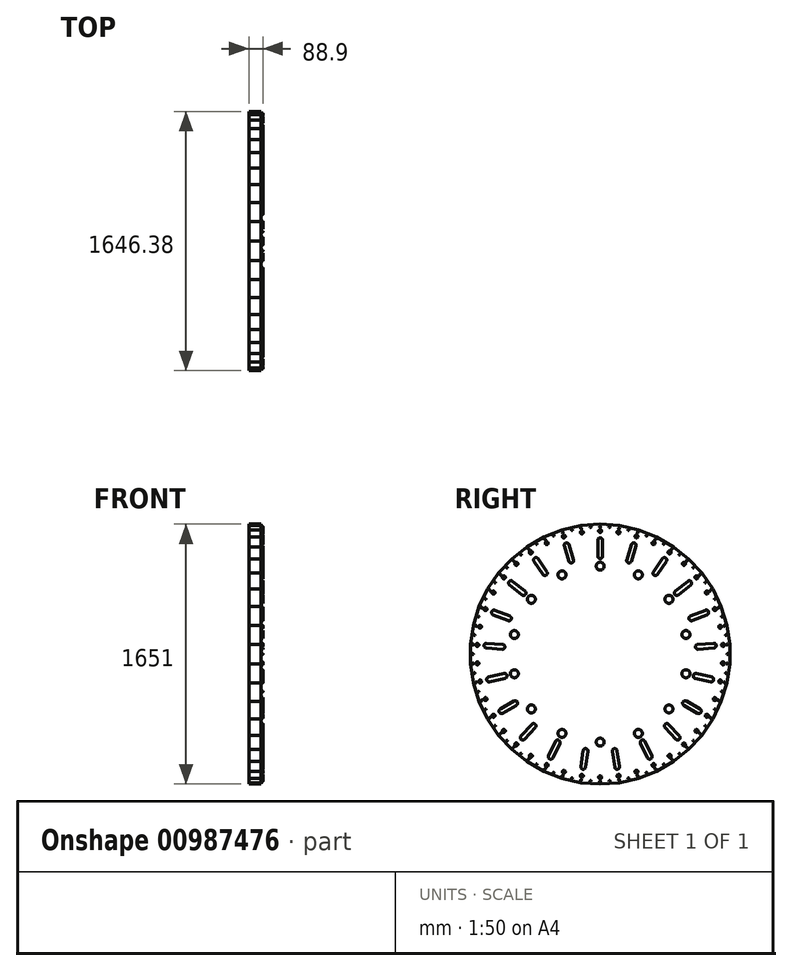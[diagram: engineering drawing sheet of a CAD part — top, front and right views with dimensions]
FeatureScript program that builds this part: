
annotation { "Feature Type Name" : "Feature", "Feature Type Description" : "" }
export const myFeature = defineFeature(function(context is Context, id is Id, definition is map)
    precondition{}
    {
        {
            var Q0;
            Q0=qCreatedBy(makeId("Right.planeOp"),FACE);
            var sketch = newSketch(context, id + "F0", { "sketchPlane" : qUnion([Q0])});
            skCircle(sketch, "E0.cCircle", {"center": v(0, 0) * mm, "radius": 825.5 * mm, "construction": true});
            skLineSegment(sketch, "E0.0", {"start": v(714.9, 412.75) * mm, "end": v(768.44, 301.59) * mm});
            skLineSegment(sketch, "E0.1", {"start": v(768.44, 301.59) * mm, "end": v(804.8, 183.7) * mm});
            skLineSegment(sketch, "E0.2", {"start": v(804.8, 183.7) * mm, "end": v(823.2, 61.69) * mm});
            skLineSegment(sketch, "E0.3", {"start": v(823.2, 61.69) * mm, "end": v(823.2, -61.69) * mm});
            skLineSegment(sketch, "E0.4", {"start": v(823.2, -61.69) * mm, "end": v(804.8, -183.7) * mm});
            skLineSegment(sketch, "E0.5", {"start": v(804.8, -183.7) * mm, "end": v(768.44, -301.59) * mm});
            skLineSegment(sketch, "E0.6", {"start": v(768.44, -301.59) * mm, "end": v(714.9, -412.75) * mm});
            skLineSegment(sketch, "E0.7", {"start": v(714.9, -412.75) * mm, "end": v(645.4, -514.7) * mm});
            skLineSegment(sketch, "E0.8", {"start": v(645.4, -514.7) * mm, "end": v(561.48, -605.13) * mm});
            skLineSegment(sketch, "E0.9", {"start": v(561.48, -605.13) * mm, "end": v(465.02, -682.06) * mm});
            skLineSegment(sketch, "E0.10", {"start": v(465.02, -682.06) * mm, "end": v(358.17, -743.75) * mm});
            skLineSegment(sketch, "E0.11", {"start": v(358.17, -743.75) * mm, "end": v(243.32, -788.83) * mm});
            skLineSegment(sketch, "E0.12", {"start": v(243.32, -788.83) * mm, "end": v(123.03, -816.28) * mm});
            skLineSegment(sketch, "E0.13", {"start": v(123.03, -816.28) * mm, "end": v(0, -825.5) * mm});
            skLineSegment(sketch, "E0.14", {"start": v(0, -825.5) * mm, "end": v(-123.03, -816.28) * mm});
            skLineSegment(sketch, "E0.15", {"start": v(-123.03, -816.28) * mm, "end": v(-243.32, -788.83) * mm});
            skLineSegment(sketch, "E0.16", {"start": v(-243.32, -788.83) * mm, "end": v(-358.17, -743.75) * mm});
            skLineSegment(sketch, "E0.17", {"start": v(-358.17, -743.75) * mm, "end": v(-465.02, -682.06) * mm});
            skLineSegment(sketch, "E0.18", {"start": v(-465.02, -682.06) * mm, "end": v(-561.48, -605.13) * mm});
            skLineSegment(sketch, "E0.19", {"start": v(-561.48, -605.13) * mm, "end": v(-645.4, -514.7) * mm});
            skLineSegment(sketch, "E0.20", {"start": v(-645.4, -514.7) * mm, "end": v(-714.9, -412.75) * mm});
            skLineSegment(sketch, "E0.21", {"start": v(-714.9, -412.75) * mm, "end": v(-768.44, -301.59) * mm});
            skLineSegment(sketch, "E0.22", {"start": v(-768.44, -301.59) * mm, "end": v(-804.8, -183.7) * mm});
            skLineSegment(sketch, "E0.23", {"start": v(-804.8, -183.7) * mm, "end": v(-823.2, -61.69) * mm});
            skLineSegment(sketch, "E0.24", {"start": v(-823.2, -61.69) * mm, "end": v(-823.2, 61.69) * mm});
            skLineSegment(sketch, "E0.25", {"start": v(-823.2, 61.69) * mm, "end": v(-804.8, 183.7) * mm});
            skLineSegment(sketch, "E0.26", {"start": v(-804.8, 183.7) * mm, "end": v(-768.44, 301.59) * mm});
            skLineSegment(sketch, "E0.27", {"start": v(-768.44, 301.59) * mm, "end": v(-714.9, 412.75) * mm});
            skLineSegment(sketch, "E0.28", {"start": v(-714.9, 412.75) * mm, "end": v(-645.4, 514.7) * mm});
            skLineSegment(sketch, "E0.29", {"start": v(-645.4, 514.7) * mm, "end": v(-561.48, 605.13) * mm});
            skLineSegment(sketch, "E0.30", {"start": v(-561.48, 605.13) * mm, "end": v(-465.02, 682.06) * mm});
            skLineSegment(sketch, "E0.31", {"start": v(-465.02, 682.06) * mm, "end": v(-358.17, 743.75) * mm});
            skLineSegment(sketch, "E0.32", {"start": v(-358.17, 743.75) * mm, "end": v(-243.32, 788.83) * mm});
            skLineSegment(sketch, "E0.33", {"start": v(-243.32, 788.83) * mm, "end": v(-123.03, 816.28) * mm});
            skLineSegment(sketch, "E0.34", {"start": v(-123.03, 816.28) * mm, "end": v(0, 825.5) * mm});
            skLineSegment(sketch, "E0.35", {"start": v(0, 825.5) * mm, "end": v(123.03, 816.28) * mm});
            skLineSegment(sketch, "E0.36", {"start": v(123.03, 816.28) * mm, "end": v(243.32, 788.83) * mm});
            skLineSegment(sketch, "E0.37", {"start": v(243.32, 788.83) * mm, "end": v(358.17, 743.75) * mm});
            skLineSegment(sketch, "E0.38", {"start": v(358.17, 743.75) * mm, "end": v(465.02, 682.06) * mm});
            skLineSegment(sketch, "E0.39", {"start": v(465.02, 682.06) * mm, "end": v(561.48, 605.13) * mm});
            skLineSegment(sketch, "E0.40", {"start": v(561.48, 605.13) * mm, "end": v(645.4, 514.7) * mm});
            skLineSegment(sketch, "E0.41", {"start": v(645.4, 514.7) * mm, "end": v(714.9, 412.75) * mm});
            skCircle(sketch, "E1", {"center": v(2658.03, 0) * mm, "radius": 825.5 * mm});
            skLineSegment(sketch, "E2", {"start": v(0, 825.5) * mm, "end": v(0, 0) * mm, "construction": true});
            skSolve(sketch);
        }
        {
            var Q0;
            Q0=makeQuery(id+"F0.imprint","IMPRINT",FACE,{"disambiguationData":[TD([[makeQuery(id+"F0.imprint","IMPRINT",EDGE,{"derivedFrom":sQuery(id+"F0.wireOp",EDGE,"E0.0")}),-1.0]])]});
            extrude(context, id + "F1", {"entities" : qUnion([Q0]), "depth" : 76.2 * mm, "offsetDistance" : 25.4 * mm});
        }
        {
            var Q0;
            Q0=makeQuery(id+"F1.opExtrude","CAP_FACE",FACE,{"disambiguationData":[OSD([sQuery(id+"F0.wireOp",EDGE,"E0.0"),sQuery(id+"F0.wireOp",EDGE,"E0.1"),sQuery(id+"F0.wireOp",EDGE,"E0.2"),sQuery(id+"F0.wireOp",EDGE,"E0.3"),sQuery(id+"F0.wireOp",EDGE,"E0.4"),sQuery(id+"F0.wireOp",EDGE,"E0.5"),sQuery(id+"F0.wireOp",EDGE,"E0.6"),sQuery(id+"F0.wireOp",EDGE,"E0.7"),sQuery(id+"F0.wireOp",EDGE,"E0.8"),sQuery(id+"F0.wireOp",EDGE,"E0.9"),sQuery(id+"F0.wireOp",EDGE,"E0.10"),sQuery(id+"F0.wireOp",EDGE,"E0.11"),sQuery(id+"F0.wireOp",EDGE,"E0.12"),sQuery(id+"F0.wireOp",EDGE,"E0.13"),sQuery(id+"F0.wireOp",EDGE,"E0.14"),sQuery(id+"F0.wireOp",EDGE,"E0.15"),sQuery(id+"F0.wireOp",EDGE,"E0.16"),sQuery(id+"F0.wireOp",EDGE,"E0.17"),sQuery(id+"F0.wireOp",EDGE,"E0.18"),sQuery(id+"F0.wireOp",EDGE,"E0.19"),sQuery(id+"F0.wireOp",EDGE,"E0.20"),sQuery(id+"F0.wireOp",EDGE,"E0.21"),sQuery(id+"F0.wireOp",EDGE,"E0.22"),sQuery(id+"F0.wireOp",EDGE,"E0.23"),sQuery(id+"F0.wireOp",EDGE,"E0.24"),sQuery(id+"F0.wireOp",EDGE,"E0.25"),sQuery(id+"F0.wireOp",EDGE,"E0.26"),sQuery(id+"F0.wireOp",EDGE,"E0.27"),sQuery(id+"F0.wireOp",EDGE,"E0.28"),sQuery(id+"F0.wireOp",EDGE,"E0.29"),sQuery(id+"F0.wireOp",EDGE,"E0.30"),sQuery(id+"F0.wireOp",EDGE,"E0.31"),sQuery(id+"F0.wireOp",EDGE,"E0.32"),sQuery(id+"F0.wireOp",EDGE,"E0.33"),sQuery(id+"F0.wireOp",EDGE,"E0.34"),sQuery(id+"F0.wireOp",EDGE,"E0.35"),sQuery(id+"F0.wireOp",EDGE,"E0.36"),sQuery(id+"F0.wireOp",EDGE,"E0.37"),sQuery(id+"F0.wireOp",EDGE,"E0.38"),sQuery(id+"F0.wireOp",EDGE,"E0.39"),sQuery(id+"F0.wireOp",EDGE,"E0.40"),sQuery(id+"F0.wireOp",EDGE,"E0.41")])],"isStart":false});
            var sketch = newSketch(context, id + "F2", { "sketchPlane" : qUnion([Q0])});
            skLineSegment(sketch, "E3", {"start": v(0, 622.3) * mm, "end": v(0, 723.9) * mm, "construction": true});
            skLineSegment(sketch, "E4", {"start": v(0, 0) * mm, "end": v(0, 622.3) * mm, "construction": true});
            skLineSegment(sketch, "E5", {"start": v(15.24, 723.9) * mm, "end": v(15.24, 622.3) * mm});
            skArc(sketch, "E6", {"start": v(-15.24, 723.9) * mm, "mid": v(0, 708.66) * mm, "end": v(15.24, 723.9) * mm, "construction": true});
            skArc(sketch, "E7", {"start": v(15.24, 723.9) * mm, "mid": v(10.78, 734.68) * mm, "end": v(0, 739.14) * mm});
            skArc(sketch, "E8", {"start": v(15.23, 622.91) * mm, "mid": v(-0.3, 637.54) * mm, "end": v(-15.24, 622.3) * mm, "construction": true});
            skArc(sketch, "E9", {"start": v(-15.24, 622.3) * mm, "mid": v(0.3, 607.06) * mm, "end": v(15.23, 622.91) * mm});
            skLineSegment(sketch, "E10.MirrorCS", {"start": v(-15.24, 723.9) * mm, "end": v(-15.24, 622.3) * mm});
            skLineSegment(sketch, "E11.1.0", {"start": v(198.81, 696.23) * mm, "end": v(168.86, 599.15) * mm});
            skArc(sketch, "E11.1.1", {"start": v(227.94, 687.25) * mm, "mid": v(217.87, 706.3) * mm, "end": v(198.81, 696.23) * mm});
            skLineSegment(sketch, "E11.1.2", {"start": v(227.94, 687.25) * mm, "end": v(197.99, 590.16) * mm});
            skArc(sketch, "E11.1.3", {"start": v(168.86, 599.15) * mm, "mid": v(179.23, 580) * mm, "end": v(198.16, 590.75) * mm});
            skLineSegment(sketch, "E11.2.0", {"start": v(395.2, 606.7) * mm, "end": v(337.96, 522.75) * mm});
            skArc(sketch, "E11.2.1", {"start": v(420.38, 589.53) * mm, "mid": v(416.37, 610.7) * mm, "end": v(395.2, 606.7) * mm});
            skLineSegment(sketch, "E11.2.2", {"start": v(420.38, 589.53) * mm, "end": v(363.15, 505.58) * mm});
            skArc(sketch, "E11.2.3", {"start": v(337.96, 522.75) * mm, "mid": v(342.22, 501.4) * mm, "end": v(363.48, 506.1) * mm});
            skLineSegment(sketch, "E11.3.0", {"start": v(556.47, 463.26) * mm, "end": v(477.03, 399.91) * mm});
            skArc(sketch, "E11.3.1", {"start": v(575.47, 439.43) * mm, "mid": v(577.88, 460.85) * mm, "end": v(556.47, 463.26) * mm});
            skLineSegment(sketch, "E11.3.2", {"start": v(575.47, 439.43) * mm, "end": v(496.04, 376.08) * mm});
            skArc(sketch, "E11.3.3", {"start": v(477.03, 399.91) * mm, "mid": v(474.81, 378.26) * mm, "end": v(496.5, 376.47) * mm});
            skLineSegment(sketch, "E11.4.0", {"start": v(668.3, 278.66) * mm, "end": v(573.71, 241.54) * mm});
            skArc(sketch, "E11.4.1", {"start": v(679.43, 250.28) * mm, "mid": v(688.05, 270.04) * mm, "end": v(668.3, 278.66) * mm});
            skLineSegment(sketch, "E11.4.2", {"start": v(679.43, 250.28) * mm, "end": v(584.85, 213.17) * mm});
            skArc(sketch, "E11.4.3", {"start": v(573.71, 241.54) * mm, "mid": v(565.21, 221.5) * mm, "end": v(585.42, 213.4) * mm});
            skLineSegment(sketch, "E11.5.0", {"start": v(720.74, 69.3) * mm, "end": v(619.42, 61.7) * mm});
            skArc(sketch, "E11.5.1", {"start": v(723.01, 38.9) * mm, "mid": v(737.07, 55.24) * mm, "end": v(720.74, 69.3) * mm});
            skLineSegment(sketch, "E11.5.2", {"start": v(723.01, 38.9) * mm, "end": v(621.7, 31.3) * mm});
            skArc(sketch, "E11.5.3", {"start": v(619.42, 61.7) * mm, "mid": v(605.39, 45.06) * mm, "end": v(622.3, 31.37) * mm});
            skLineSegment(sketch, "E11.6.0", {"start": v(709.14, -146.23) * mm, "end": v(610.09, -123.62) * mm});
            skArc(sketch, "E11.6.1", {"start": v(702.36, -175.94) * mm, "mid": v(720.6, -164.47) * mm, "end": v(709.14, -146.23) * mm});
            skLineSegment(sketch, "E11.6.2", {"start": v(702.36, -175.94) * mm, "end": v(603.3, -153.33) * mm});
            skArc(sketch, "E11.6.3", {"start": v(610.09, -123.62) * mm, "mid": v(591.77, -135.38) * mm, "end": v(603.9, -153.46) * mm});
            skLineSegment(sketch, "E11.7.0", {"start": v(634.54, -348.75) * mm, "end": v(546.55, -297.95) * mm});
            skArc(sketch, "E11.7.1", {"start": v(619.3, -375.15) * mm, "mid": v(640.11, -369.57) * mm, "end": v(634.54, -348.75) * mm});
            skLineSegment(sketch, "E11.7.2", {"start": v(619.3, -375.15) * mm, "end": v(531.3, -324.35) * mm});
            skArc(sketch, "E11.7.3", {"start": v(546.55, -297.95) * mm, "mid": v(525.58, -303.8) * mm, "end": v(531.85, -324.64) * mm});
            skLineSegment(sketch, "E11.8.0", {"start": v(503.55, -520.3) * mm, "end": v(434.44, -445.81) * mm});
            skArc(sketch, "E11.8.1", {"start": v(481.2, -541.02) * mm, "mid": v(502.74, -541.83) * mm, "end": v(503.55, -520.3) * mm});
            skLineSegment(sketch, "E11.8.2", {"start": v(481.2, -541.02) * mm, "end": v(412.1, -466.54) * mm});
            skArc(sketch, "E11.8.3", {"start": v(434.44, -445.81) * mm, "mid": v(412.68, -445.22) * mm, "end": v(412.53, -466.99) * mm});
            skLineSegment(sketch, "E11.9.0", {"start": v(327.82, -645.6) * mm, "end": v(283.74, -554.06) * mm});
            skArc(sketch, "E11.9.1", {"start": v(300.36, -658.82) * mm, "mid": v(320.7, -665.94) * mm, "end": v(327.82, -645.6) * mm});
            skLineSegment(sketch, "E11.9.2", {"start": v(300.36, -658.82) * mm, "end": v(256.28, -567.29) * mm});
            skArc(sketch, "E11.9.3", {"start": v(283.74, -554.06) * mm, "mid": v(263.12, -547.08) * mm, "end": v(256.55, -567.83) * mm});
            skLineSegment(sketch, "E11.10.0", {"start": v(122.96, -713.54) * mm, "end": v(107.82, -613.08) * mm});
            skArc(sketch, "E11.10.1", {"start": v(92.82, -718.09) * mm, "mid": v(110.16, -730.88) * mm, "end": v(122.96, -713.54) * mm});
            skLineSegment(sketch, "E11.10.2", {"start": v(92.82, -718.09) * mm, "end": v(77.68, -617.62) * mm});
            skArc(sketch, "E11.10.3", {"start": v(107.82, -613.08) * mm, "mid": v(90.17, -600.33) * mm, "end": v(77.78, -618.23) * mm});
            skLineSegment(sketch, "E11.11.0", {"start": v(-92.82, -718.09) * mm, "end": v(-77.68, -617.62) * mm});
            skArc(sketch, "E11.11.1", {"start": v(-122.96, -713.54) * mm, "mid": v(-110.16, -730.88) * mm, "end": v(-92.82, -718.09) * mm});
            skLineSegment(sketch, "E11.11.2", {"start": v(-122.96, -713.54) * mm, "end": v(-107.82, -613.08) * mm});
            skArc(sketch, "E11.11.3", {"start": v(-77.68, -617.62) * mm, "mid": v(-90.78, -600.24) * mm, "end": v(-107.9, -613.69) * mm});
            skLineSegment(sketch, "E11.12.0", {"start": v(-300.36, -658.82) * mm, "end": v(-256.28, -567.29) * mm});
            skArc(sketch, "E11.12.1", {"start": v(-327.82, -645.6) * mm, "mid": v(-320.7, -665.94) * mm, "end": v(-300.36, -658.82) * mm});
            skLineSegment(sketch, "E11.12.2", {"start": v(-327.82, -645.6) * mm, "end": v(-283.74, -554.06) * mm});
            skArc(sketch, "E11.12.3", {"start": v(-256.28, -567.29) * mm, "mid": v(-263.67, -546.81) * mm, "end": v(-284, -554.62) * mm});
            skLineSegment(sketch, "E11.13.0", {"start": v(-481.2, -541.02) * mm, "end": v(-412.1, -466.54) * mm});
            skArc(sketch, "E11.13.1", {"start": v(-503.55, -520.3) * mm, "mid": v(-502.74, -541.83) * mm, "end": v(-481.2, -541.02) * mm});
            skLineSegment(sketch, "E11.13.2", {"start": v(-503.55, -520.3) * mm, "end": v(-434.44, -445.81) * mm});
            skArc(sketch, "E11.13.3", {"start": v(-412.1, -466.54) * mm, "mid": v(-413.13, -444.8) * mm, "end": v(-434.85, -446.27) * mm});
            skLineSegment(sketch, "E11.14.0", {"start": v(-619.3, -375.15) * mm, "end": v(-531.3, -324.35) * mm});
            skArc(sketch, "E11.14.1", {"start": v(-634.54, -348.75) * mm, "mid": v(-640.11, -369.57) * mm, "end": v(-619.3, -375.15) * mm});
            skLineSegment(sketch, "E11.14.2", {"start": v(-634.54, -348.75) * mm, "end": v(-546.55, -297.95) * mm});
            skArc(sketch, "E11.14.3", {"start": v(-531.3, -324.35) * mm, "mid": v(-525.89, -303.27) * mm, "end": v(-547.07, -298.27) * mm});
            skLineSegment(sketch, "E11.15.0", {"start": v(-702.36, -175.94) * mm, "end": v(-603.3, -153.33) * mm});
            skArc(sketch, "E11.15.1", {"start": v(-709.14, -146.23) * mm, "mid": v(-720.6, -164.47) * mm, "end": v(-702.36, -175.94) * mm});
            skLineSegment(sketch, "E11.15.2", {"start": v(-709.14, -146.23) * mm, "end": v(-610.09, -123.62) * mm});
            skArc(sketch, "E11.15.3", {"start": v(-603.3, -153.33) * mm, "mid": v(-591.91, -134.79) * mm, "end": v(-610.68, -123.77) * mm});
            skLineSegment(sketch, "E11.16.0", {"start": v(-723.01, 38.9) * mm, "end": v(-621.7, 31.3) * mm});
            skArc(sketch, "E11.16.1", {"start": v(-720.74, 69.3) * mm, "mid": v(-737.07, 55.24) * mm, "end": v(-723.01, 38.9) * mm});
            skLineSegment(sketch, "E11.16.2", {"start": v(-720.74, 69.3) * mm, "end": v(-619.42, 61.7) * mm});
            skArc(sketch, "E11.16.3", {"start": v(-621.7, 31.3) * mm, "mid": v(-605.34, 45.67) * mm, "end": v(-620.03, 61.74) * mm});
            skLineSegment(sketch, "E11.17.0", {"start": v(-679.43, 250.28) * mm, "end": v(-584.85, 213.17) * mm});
            skArc(sketch, "E11.17.1", {"start": v(-668.3, 278.66) * mm, "mid": v(-688.05, 270.04) * mm, "end": v(-679.43, 250.28) * mm});
            skLineSegment(sketch, "E11.17.2", {"start": v(-668.3, 278.66) * mm, "end": v(-573.71, 241.54) * mm});
            skArc(sketch, "E11.17.3", {"start": v(-584.85, 213.17) * mm, "mid": v(-564.99, 222.07) * mm, "end": v(-574.3, 241.75) * mm});
            skLineSegment(sketch, "E11.18.0", {"start": v(-575.47, 439.43) * mm, "end": v(-496.04, 376.08) * mm});
            skArc(sketch, "E11.18.1", {"start": v(-556.47, 463.26) * mm, "mid": v(-577.88, 460.85) * mm, "end": v(-575.47, 439.43) * mm});
            skLineSegment(sketch, "E11.18.2", {"start": v(-556.47, 463.26) * mm, "end": v(-477.03, 399.91) * mm});
            skArc(sketch, "E11.18.3", {"start": v(-496.04, 376.08) * mm, "mid": v(-474.43, 378.74) * mm, "end": v(-477.52, 400.29) * mm});
            skLineSegment(sketch, "E11.19.0", {"start": v(-420.38, 589.53) * mm, "end": v(-363.15, 505.58) * mm});
            skArc(sketch, "E11.19.1", {"start": v(-395.2, 606.7) * mm, "mid": v(-416.37, 610.7) * mm, "end": v(-420.38, 589.53) * mm});
            skLineSegment(sketch, "E11.19.2", {"start": v(-395.2, 606.7) * mm, "end": v(-337.96, 522.75) * mm});
            skArc(sketch, "E11.19.3", {"start": v(-363.15, 505.58) * mm, "mid": v(-341.72, 501.75) * mm, "end": v(-338.32, 523.25) * mm});
            skLineSegment(sketch, "E11.20.0", {"start": v(-227.94, 687.25) * mm, "end": v(-197.99, 590.16) * mm});
            skArc(sketch, "E11.20.1", {"start": v(-198.81, 696.23) * mm, "mid": v(-217.87, 706.3) * mm, "end": v(-227.94, 687.25) * mm});
            skLineSegment(sketch, "E11.20.2", {"start": v(-198.81, 696.23) * mm, "end": v(-168.86, 599.15) * mm});
            skArc(sketch, "E11.20.3", {"start": v(-197.99, 590.16) * mm, "mid": v(-178.64, 580.18) * mm, "end": v(-169.06, 599.73) * mm});
            skPoint(sketch, "E11.center", {"position": v(0, 0) * mm});
            skLineSegment(sketch, "E11.anchor1", {"start": v(0, 0) * mm, "end": v(-15.24, 622.3) * mm, "construction": true});
            skLineSegment(sketch, "E11.anchor2", {"start": v(0, 0) * mm, "end": v(-197.99, 590.16) * mm, "construction": true});
            skLineSegment(sketch, "E12", {"start": v(0, 723.9) * mm, "end": v(0, 825.5) * mm, "construction": true});
            skArc(sketch, "E13", {"start": v(0, 739.14) * mm, "mid": v(-10.78, 734.68) * mm, "end": v(-15.24, 723.9) * mm});
            skCircle(sketch, "E14.1.0", {"center": v(-116.6, 773.58) * mm, "radius": 9.53 * mm});
            skCircle(sketch, "E14.2.0", {"center": v(-230.6, 747.56) * mm, "radius": 9.53 * mm});
            skCircle(sketch, "E14.3.0", {"center": v(-339.44, 704.85) * mm, "radius": 9.53 * mm});
            skCircle(sketch, "E14.4.0", {"center": v(-440.7, 646.38) * mm, "radius": 9.53 * mm});
            skCircle(sketch, "E14.5.0", {"center": v(-532.11, 573.48) * mm, "radius": 9.53 * mm});
            skCircle(sketch, "E14.6.0", {"center": v(-611.64, 487.77) * mm, "radius": 9.53 * mm});
            skCircle(sketch, "E14.7.0", {"center": v(-677.5, 391.16) * mm, "radius": 9.53 * mm});
            skCircle(sketch, "E14.8.0", {"center": v(-728.24, 285.81) * mm, "radius": 9.53 * mm});
            skCircle(sketch, "E14.9.0", {"center": v(-762.7, 174.08) * mm, "radius": 9.53 * mm});
            skCircle(sketch, "E14.10.0", {"center": v(-780.13, 58.46) * mm, "radius": 9.53 * mm});
            skCircle(sketch, "E14.11.0", {"center": v(-780.13, -58.46) * mm, "radius": 9.53 * mm});
            skCircle(sketch, "E14.12.0", {"center": v(-762.7, -174.08) * mm, "radius": 9.53 * mm});
            skCircle(sketch, "E14.13.0", {"center": v(-728.24, -285.81) * mm, "radius": 9.53 * mm});
            skCircle(sketch, "E14.14.0", {"center": v(-677.5, -391.16) * mm, "radius": 9.53 * mm});
            skCircle(sketch, "E14.15.0", {"center": v(-611.64, -487.77) * mm, "radius": 9.53 * mm});
            skCircle(sketch, "E14.16.0", {"center": v(-532.11, -573.48) * mm, "radius": 9.53 * mm});
            skCircle(sketch, "E14.17.0", {"center": v(-440.7, -646.38) * mm, "radius": 9.53 * mm});
            skCircle(sketch, "E14.18.0", {"center": v(-339.44, -704.85) * mm, "radius": 9.53 * mm});
            skCircle(sketch, "E14.19.0", {"center": v(-230.6, -747.56) * mm, "radius": 9.53 * mm});
            skCircle(sketch, "E14.20.0", {"center": v(-116.6, -773.58) * mm, "radius": 9.53 * mm});
            skCircle(sketch, "E14.21.0", {"center": v(0, -782.32) * mm, "radius": 9.53 * mm});
            skCircle(sketch, "E14.22.0", {"center": v(116.6, -773.58) * mm, "radius": 9.53 * mm});
            skCircle(sketch, "E14.23.0", {"center": v(230.6, -747.56) * mm, "radius": 9.53 * mm});
            skCircle(sketch, "E14.24.0", {"center": v(339.44, -704.85) * mm, "radius": 9.53 * mm});
            skCircle(sketch, "E14.25.0", {"center": v(440.7, -646.38) * mm, "radius": 9.53 * mm});
            skCircle(sketch, "E14.26.0", {"center": v(532.11, -573.48) * mm, "radius": 9.53 * mm});
            skCircle(sketch, "E14.27.0", {"center": v(611.64, -487.77) * mm, "radius": 9.53 * mm});
            skCircle(sketch, "E14.28.0", {"center": v(677.5, -391.16) * mm, "radius": 9.53 * mm});
            skCircle(sketch, "E14.29.0", {"center": v(728.24, -285.81) * mm, "radius": 9.53 * mm});
            skCircle(sketch, "E14.30.0", {"center": v(762.7, -174.08) * mm, "radius": 9.53 * mm});
            skCircle(sketch, "E14.31.0", {"center": v(780.13, -58.46) * mm, "radius": 9.53 * mm});
            skCircle(sketch, "E14.32.0", {"center": v(780.13, 58.46) * mm, "radius": 9.53 * mm});
            skCircle(sketch, "E14.33.0", {"center": v(762.7, 174.08) * mm, "radius": 9.53 * mm});
            skCircle(sketch, "E14.34.0", {"center": v(728.24, 285.81) * mm, "radius": 9.53 * mm});
            skCircle(sketch, "E14.35.0", {"center": v(677.5, 391.16) * mm, "radius": 9.53 * mm});
            skCircle(sketch, "E14.36.0", {"center": v(611.64, 487.77) * mm, "radius": 9.53 * mm});
            skCircle(sketch, "E14.37.0", {"center": v(532.11, 573.48) * mm, "radius": 9.53 * mm});
            skCircle(sketch, "E14.38.0", {"center": v(440.7, 646.38) * mm, "radius": 9.53 * mm});
            skCircle(sketch, "E14.39.0", {"center": v(339.44, 704.85) * mm, "radius": 9.53 * mm});
            skCircle(sketch, "E14.40.0", {"center": v(230.6, 747.56) * mm, "radius": 9.53 * mm});
            skCircle(sketch, "E14.41.0", {"center": v(116.6, 773.58) * mm, "radius": 9.53 * mm});
            skCircle(sketch, "E15", {"center": v(0, 558.8) * mm, "radius": 25.4 * mm});
            skCircle(sketch, "E16.1.0", {"center": v(-242.45, 503.46) * mm, "radius": 25.4 * mm});
            skCircle(sketch, "E16.2.0", {"center": v(-436.89, 348.4) * mm, "radius": 25.4 * mm});
            skCircle(sketch, "E16.3.0", {"center": v(-544.79, 124.34) * mm, "radius": 25.4 * mm});
            skCircle(sketch, "E16.4.0", {"center": v(-544.79, -124.34) * mm, "radius": 25.4 * mm});
            skCircle(sketch, "E16.5.0", {"center": v(-436.89, -348.4) * mm, "radius": 25.4 * mm});
            skCircle(sketch, "E16.6.0", {"center": v(-242.45, -503.46) * mm, "radius": 25.4 * mm});
            skCircle(sketch, "E16.7.0", {"center": v(0, -558.8) * mm, "radius": 25.4 * mm});
            skCircle(sketch, "E16.8.0", {"center": v(242.45, -503.46) * mm, "radius": 25.4 * mm});
            skCircle(sketch, "E16.9.0", {"center": v(436.89, -348.4) * mm, "radius": 25.4 * mm});
            skCircle(sketch, "E16.10.0", {"center": v(544.79, -124.34) * mm, "radius": 25.4 * mm});
            skCircle(sketch, "E16.11.0", {"center": v(544.79, 124.34) * mm, "radius": 25.4 * mm});
            skCircle(sketch, "E16.12.0", {"center": v(436.89, 348.4) * mm, "radius": 25.4 * mm});
            skCircle(sketch, "E16.13.0", {"center": v(242.45, 503.46) * mm, "radius": 25.4 * mm});
            skCircle(sketch, "E17", {"center": v(0, 808.67) * mm, "radius": 3.18 * mm});
            skArc(sketch, "E18", {"start": v(0, 791.85) * mm, "mid": v(-9.53, 782.32) * mm, "end": v(0, 772.8) * mm});
            skArc(sketch, "E19", {"start": v(0, 772.8) * mm, "mid": v(9.53, 782.32) * mm, "end": v(0, 791.85) * mm});
            skCircle(sketch, "E20.1.0", {"center": v(-60.43, 806.41) * mm, "radius": 3.18 * mm});
            skCircle(sketch, "E20.2.0", {"center": v(-120.53, 799.64) * mm, "radius": 3.18 * mm});
            skCircle(sketch, "E20.3.0", {"center": v(-179.95, 788.4) * mm, "radius": 3.18 * mm});
            skCircle(sketch, "E20.4.0", {"center": v(-238.36, 772.75) * mm, "radius": 3.18 * mm});
            skCircle(sketch, "E20.5.0", {"center": v(-295.44, 752.77) * mm, "radius": 3.18 * mm});
            skCircle(sketch, "E20.6.0", {"center": v(-350.87, 728.59) * mm, "radius": 3.18 * mm});
            skCircle(sketch, "E20.7.0", {"center": v(-404.34, 700.33) * mm, "radius": 3.18 * mm});
            skCircle(sketch, "E20.8.0", {"center": v(-455.54, 668.16) * mm, "radius": 3.18 * mm});
            skCircle(sketch, "E20.9.0", {"center": v(-504.2, 632.25) * mm, "radius": 3.18 * mm});
            skCircle(sketch, "E20.10.0", {"center": v(-550.04, 592.8) * mm, "radius": 3.18 * mm});
            skCircle(sketch, "E20.11.0", {"center": v(-592.8, 550.04) * mm, "radius": 3.18 * mm});
            skCircle(sketch, "E20.12.0", {"center": v(-632.25, 504.2) * mm, "radius": 3.18 * mm});
            skCircle(sketch, "E20.13.0", {"center": v(-668.16, 455.54) * mm, "radius": 3.18 * mm});
            skCircle(sketch, "E20.14.0", {"center": v(-700.33, 404.34) * mm, "radius": 3.18 * mm});
            skCircle(sketch, "E20.15.0", {"center": v(-728.59, 350.87) * mm, "radius": 3.18 * mm});
            skCircle(sketch, "E20.16.0", {"center": v(-752.77, 295.44) * mm, "radius": 3.18 * mm});
            skCircle(sketch, "E20.17.0", {"center": v(-772.75, 238.36) * mm, "radius": 3.18 * mm});
            skCircle(sketch, "E20.18.0", {"center": v(-788.4, 179.95) * mm, "radius": 3.18 * mm});
            skCircle(sketch, "E20.19.0", {"center": v(-799.64, 120.53) * mm, "radius": 3.18 * mm});
            skCircle(sketch, "E20.20.0", {"center": v(-806.41, 60.43) * mm, "radius": 3.18 * mm});
            skCircle(sketch, "E20.21.0", {"center": v(-808.67, 0) * mm, "radius": 3.18 * mm});
            skCircle(sketch, "E20.22.0", {"center": v(-806.41, -60.43) * mm, "radius": 3.18 * mm});
            skCircle(sketch, "E20.23.0", {"center": v(-799.64, -120.53) * mm, "radius": 3.18 * mm});
            skCircle(sketch, "E20.24.0", {"center": v(-788.4, -179.95) * mm, "radius": 3.18 * mm});
            skCircle(sketch, "E20.25.0", {"center": v(-772.75, -238.36) * mm, "radius": 3.18 * mm});
            skCircle(sketch, "E20.26.0", {"center": v(-752.77, -295.44) * mm, "radius": 3.18 * mm});
            skCircle(sketch, "E20.27.0", {"center": v(-728.59, -350.87) * mm, "radius": 3.18 * mm});
            skCircle(sketch, "E20.28.0", {"center": v(-700.33, -404.34) * mm, "radius": 3.18 * mm});
            skCircle(sketch, "E20.29.0", {"center": v(-668.16, -455.54) * mm, "radius": 3.18 * mm});
            skCircle(sketch, "E20.30.0", {"center": v(-632.25, -504.2) * mm, "radius": 3.18 * mm});
            skCircle(sketch, "E20.31.0", {"center": v(-592.8, -550.04) * mm, "radius": 3.18 * mm});
            skCircle(sketch, "E20.32.0", {"center": v(-550.04, -592.8) * mm, "radius": 3.18 * mm});
            skCircle(sketch, "E20.33.0", {"center": v(-504.2, -632.25) * mm, "radius": 3.18 * mm});
            skCircle(sketch, "E20.34.0", {"center": v(-455.54, -668.16) * mm, "radius": 3.18 * mm});
            skCircle(sketch, "E20.35.0", {"center": v(-404.34, -700.33) * mm, "radius": 3.18 * mm});
            skCircle(sketch, "E20.36.0", {"center": v(-350.87, -728.59) * mm, "radius": 3.18 * mm});
            skCircle(sketch, "E20.37.0", {"center": v(-295.44, -752.77) * mm, "radius": 3.18 * mm});
            skCircle(sketch, "E20.38.0", {"center": v(-238.36, -772.75) * mm, "radius": 3.18 * mm});
            skCircle(sketch, "E20.39.0", {"center": v(-179.95, -788.4) * mm, "radius": 3.18 * mm});
            skCircle(sketch, "E20.40.0", {"center": v(-120.53, -799.64) * mm, "radius": 3.18 * mm});
            skCircle(sketch, "E20.41.0", {"center": v(-60.43, -806.41) * mm, "radius": 3.18 * mm});
            skCircle(sketch, "E20.42.0", {"center": v(0, -808.67) * mm, "radius": 3.18 * mm});
            skCircle(sketch, "E20.43.0", {"center": v(60.43, -806.41) * mm, "radius": 3.17 * mm});
            skCircle(sketch, "E20.44.0", {"center": v(120.53, -799.64) * mm, "radius": 3.18 * mm});
            skCircle(sketch, "E20.45.0", {"center": v(179.95, -788.4) * mm, "radius": 3.18 * mm});
            skCircle(sketch, "E20.46.0", {"center": v(238.36, -772.75) * mm, "radius": 3.18 * mm});
            skCircle(sketch, "E20.47.0", {"center": v(295.44, -752.77) * mm, "radius": 3.18 * mm});
            skCircle(sketch, "E20.48.0", {"center": v(350.87, -728.59) * mm, "radius": 3.18 * mm});
            skCircle(sketch, "E20.49.0", {"center": v(404.34, -700.33) * mm, "radius": 3.18 * mm});
            skCircle(sketch, "E20.50.0", {"center": v(455.54, -668.16) * mm, "radius": 3.18 * mm});
            skCircle(sketch, "E20.51.0", {"center": v(504.2, -632.25) * mm, "radius": 3.18 * mm});
            skCircle(sketch, "E20.52.0", {"center": v(550.04, -592.8) * mm, "radius": 3.18 * mm});
            skCircle(sketch, "E20.53.0", {"center": v(592.8, -550.04) * mm, "radius": 3.18 * mm});
            skCircle(sketch, "E20.54.0", {"center": v(632.25, -504.2) * mm, "radius": 3.18 * mm});
            skCircle(sketch, "E20.55.0", {"center": v(668.16, -455.54) * mm, "radius": 3.18 * mm});
            skCircle(sketch, "E20.56.0", {"center": v(700.33, -404.34) * mm, "radius": 3.18 * mm});
            skCircle(sketch, "E20.57.0", {"center": v(728.59, -350.87) * mm, "radius": 3.18 * mm});
            skCircle(sketch, "E20.58.0", {"center": v(752.77, -295.44) * mm, "radius": 3.18 * mm});
            skCircle(sketch, "E20.59.0", {"center": v(772.75, -238.36) * mm, "radius": 3.18 * mm});
            skCircle(sketch, "E20.60.0", {"center": v(788.4, -179.95) * mm, "radius": 3.18 * mm});
            skCircle(sketch, "E20.61.0", {"center": v(799.64, -120.53) * mm, "radius": 3.18 * mm});
            skCircle(sketch, "E20.62.0", {"center": v(806.41, -60.43) * mm, "radius": 3.18 * mm});
            skCircle(sketch, "E20.63.0", {"center": v(808.67, 0) * mm, "radius": 3.18 * mm});
            skCircle(sketch, "E20.64.0", {"center": v(806.41, 60.43) * mm, "radius": 3.18 * mm});
            skCircle(sketch, "E20.65.0", {"center": v(799.64, 120.53) * mm, "radius": 3.18 * mm});
            skCircle(sketch, "E20.66.0", {"center": v(788.4, 179.95) * mm, "radius": 3.18 * mm});
            skCircle(sketch, "E20.67.0", {"center": v(772.75, 238.36) * mm, "radius": 3.18 * mm});
            skCircle(sketch, "E20.68.0", {"center": v(752.77, 295.44) * mm, "radius": 3.18 * mm});
            skCircle(sketch, "E20.69.0", {"center": v(728.59, 350.87) * mm, "radius": 3.18 * mm});
            skCircle(sketch, "E20.70.0", {"center": v(700.33, 404.34) * mm, "radius": 3.18 * mm});
            skCircle(sketch, "E20.71.0", {"center": v(668.16, 455.54) * mm, "radius": 3.18 * mm});
            skCircle(sketch, "E20.72.0", {"center": v(632.25, 504.2) * mm, "radius": 3.18 * mm});
            skCircle(sketch, "E20.73.0", {"center": v(592.8, 550.04) * mm, "radius": 3.18 * mm});
            skCircle(sketch, "E20.74.0", {"center": v(550.04, 592.8) * mm, "radius": 3.18 * mm});
            skCircle(sketch, "E20.75.0", {"center": v(504.2, 632.25) * mm, "radius": 3.18 * mm});
            skCircle(sketch, "E20.76.0", {"center": v(455.54, 668.16) * mm, "radius": 3.18 * mm});
            skCircle(sketch, "E20.77.0", {"center": v(404.34, 700.33) * mm, "radius": 3.18 * mm});
            skCircle(sketch, "E20.78.0", {"center": v(350.87, 728.59) * mm, "radius": 3.18 * mm});
            skCircle(sketch, "E20.79.0", {"center": v(295.44, 752.77) * mm, "radius": 3.18 * mm});
            skCircle(sketch, "E20.80.0", {"center": v(238.36, 772.75) * mm, "radius": 3.18 * mm});
            skCircle(sketch, "E20.81.0", {"center": v(179.95, 788.4) * mm, "radius": 3.18 * mm});
            skCircle(sketch, "E20.82.0", {"center": v(120.53, 799.64) * mm, "radius": 3.18 * mm});
            skCircle(sketch, "E20.83.0", {"center": v(60.43, 806.41) * mm, "radius": 3.18 * mm});
            skSolve(sketch);
        }
        {
            var Q0;
            Q0 = qSketchRegion(id + "F2", true);
            extrude(context, id + "F3", {"entities" : qUnion([Q0]), "operationType" : NewBodyOperationType.ADD, "depth" : 12.7 * mm, "offsetDistance" : 25.4 * mm});
        }
    });
